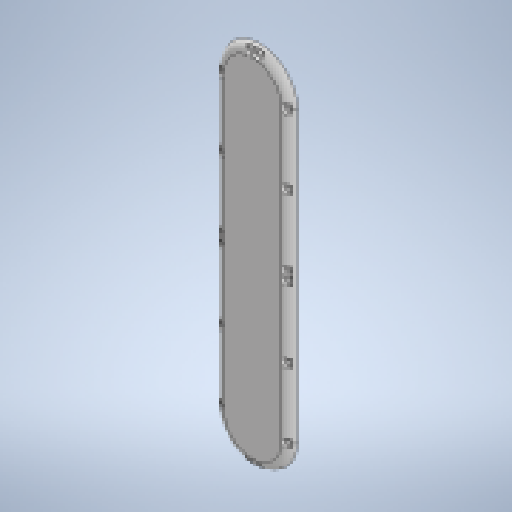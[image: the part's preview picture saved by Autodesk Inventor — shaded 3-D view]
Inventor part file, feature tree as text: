
AUTODESK INVENTOR PART (.ipt)
format: ipt  version: 2024 (Build 280153000, 153)  size: 302,592 bytes
history: native  units: in
note: dims shown in document units (in); Inventor stores cm internally (conversion verified against a paired STEP export)
features: reference x22, other x4, extrude x2, sketch x2, fillet x1, projected_geometry x1
ambient origin geometry x8: Origin, YZ Plane, XZ Plane, XY Plane, X Axis, Y Axis, Z Axis, Center Point
bodies: Solid1 (feature_tree)
feature tree (32):
  extrude  "Extrusion1"  Depth=0.0787in
  fillet  "Fillet1"  Radius=0.0787in
  extrude  "Extrusion2"  Depth=0.0787in
  sketch  "Sketch1"  dims[d0=0.2362in d1=0.0in d2=0.0787in d3=0.0787in]
  reference  "Reference1"
  reference  "Reference2"
  reference  "Reference3"
  reference  "Reference4"
  reference  "Reference5"
  reference  "Reference6"
  reference  "Reference7"
  reference  "Reference8"
  reference  "Reference9"
  reference  "Reference10"
  reference  "Reference11"
  reference  "Reference12"
  reference  "Reference13"
  reference  "Reference14"
  reference  "Reference15"
  reference  "Reference16"
  reference  "Reference17"
  reference  "Reference18"
  reference  "Reference19"
  reference  "Reference20"
  reference  "Reference21"
  reference  "Reference22"
  sketch  "Sketch2"  dims[d4=0.0787in d5=0.0787in d6=0.0787in d7=0.0787in d8=0.0787in d9=0.0787in d10=0.0787in d11=0.0787in d12=0.0787in d13=0.0787in d14=0.0787in d15=0.0787in d16=0.0787in d17=0.0787in d18=0.1181in d19=0.0in d20=0.2756in]
  projected_geometry  "Projected Loop1"
  other  "<userpath>\Downloads\AR4 CAD Files\AR4 Main Assembly\AR4 Main Assembly.iam"
  other  "AR4 Main Assembly.iam"
  other  "J2 Side Cover Upper_80"
  other  "J2 Side Cover Lower_81"
